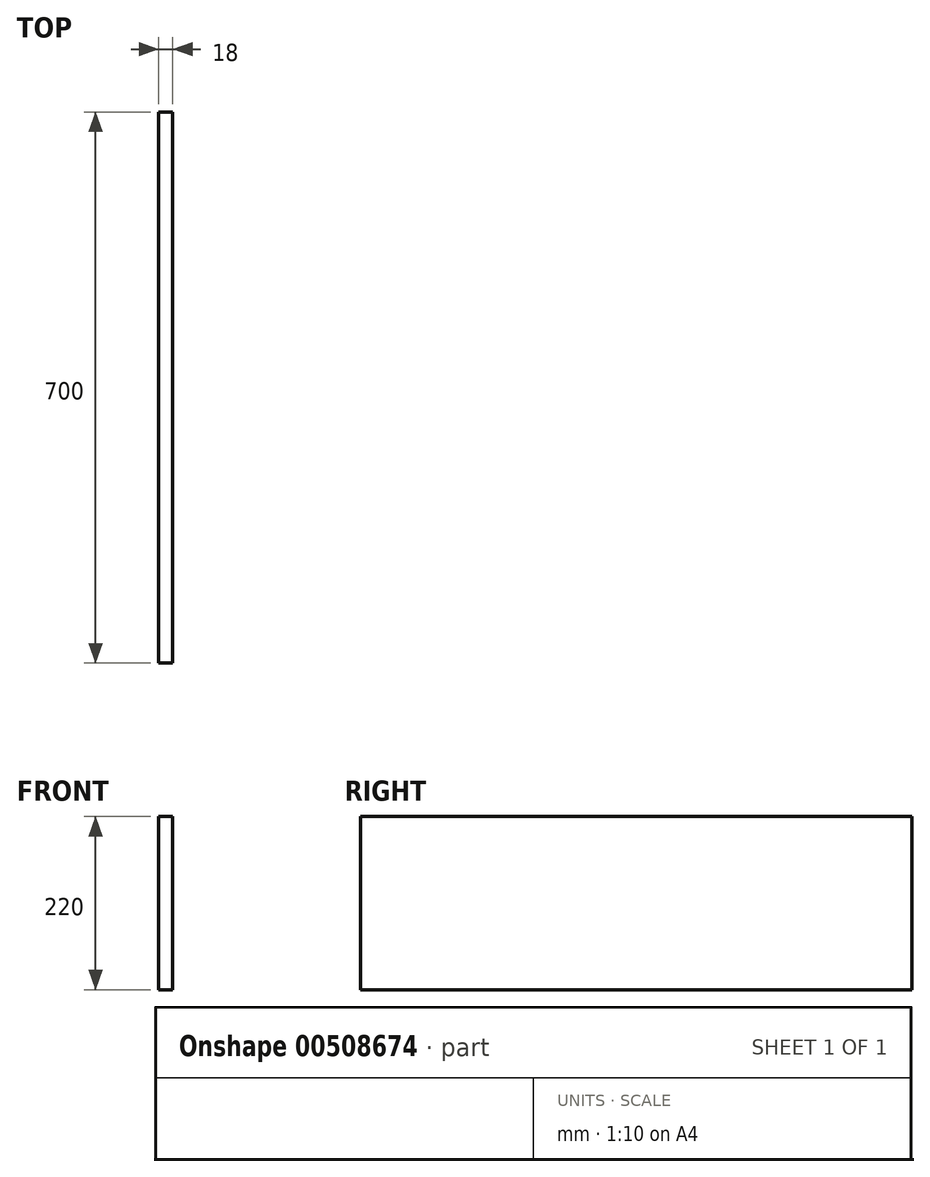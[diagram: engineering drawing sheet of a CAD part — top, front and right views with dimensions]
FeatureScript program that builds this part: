
annotation { "Feature Type Name" : "Feature", "Feature Type Description" : "" }
export const myFeature = defineFeature(function(context is Context, id is Id, definition is map)
    precondition{}
    {
        {
            var Q0;
            Q0=qCreatedBy(makeId("Front.planeOp"),FACE);
            var sketch = newSketch(context, id + "F0", { "sketchPlane" : qUnion([Q0])});
            skLineSegment(sketch, "E0.bottom", {"start": v(9, -110) * mm, "end": v(-9, -110) * mm});
            skLineSegment(sketch, "E0.top", {"start": v(9, 110) * mm, "end": v(-9, 110) * mm});
            skLineSegment(sketch, "E0.left", {"start": v(9, -110) * mm, "end": v(9, 110) * mm});
            skLineSegment(sketch, "E0.right", {"start": v(-9, -110) * mm, "end": v(-9, 110) * mm});
            skPoint(sketch, "E0.middle", {"position": v(0, 0) * mm});
            skSolve(sketch);
        }
        {
            var Q0;
            Q0=makeQuery(id+"F0.imprint","IMPRINT",FACE,{"disambiguationData":[TD([[makeQuery(id+"F0.imprint","IMPRINT",EDGE,{"derivedFrom":sQuery(id+"F0.wireOp",EDGE,"E0.bottom")}),-1.0]])]});
            extrude(context, id + "F1", {"entities" : qUnion([Q0]), "oppositeDirection" : true, "depth" : 700 * mm});
        }
    });
